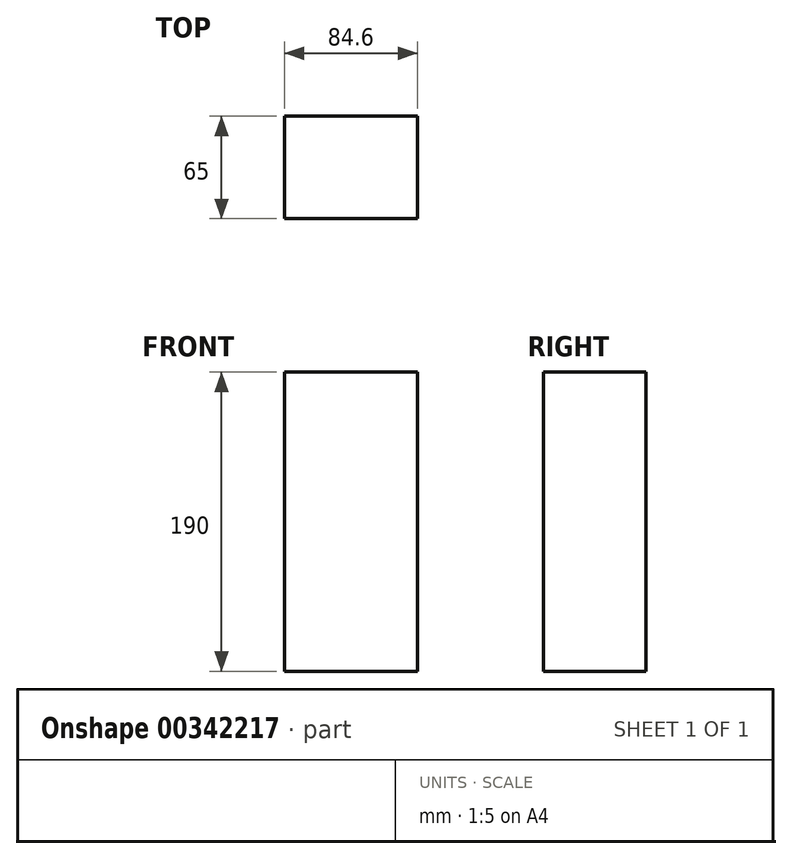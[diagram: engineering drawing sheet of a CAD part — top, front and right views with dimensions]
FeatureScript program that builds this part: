
annotation { "Feature Type Name" : "Feature", "Feature Type Description" : "" }
export const myFeature = defineFeature(function(context is Context, id is Id, definition is map)
    precondition{}
    {
        {
            var Q0;
            Q0=qCreatedBy(makeId("Top.planeOp"),FACE);
            var sketch = newSketch(context, id + "F0", { "sketchPlane" : qUnion([Q0])});
            skLineSegment(sketch, "E0.bottom", {"start": v(42.3, -32.5) * mm, "end": v(-42.3, -32.5) * mm});
            skLineSegment(sketch, "E0.top", {"start": v(42.3, 32.5) * mm, "end": v(-42.3, 32.5) * mm});
            skLineSegment(sketch, "E0.left", {"start": v(42.3, -32.5) * mm, "end": v(42.3, 32.5) * mm});
            skLineSegment(sketch, "E0.right", {"start": v(-42.3, -32.5) * mm, "end": v(-42.3, 32.5) * mm});
            skPoint(sketch, "E0.middle", {"position": v(0, 0) * mm});
            skSolve(sketch);
        }
        {
            var Q0;
            Q0=makeQuery(id+"F0.imprint","IMPRINT",FACE,{"disambiguationData":[TD([[makeQuery(id+"F0.imprint","IMPRINT",EDGE,{"derivedFrom":sQuery(id+"F0.wireOp",EDGE,"E0.bottom")}),-1.0]])]});
            extrude(context, id + "F1", {"entities" : qUnion([Q0]), "depth" : 190 * mm});
        }
    });
